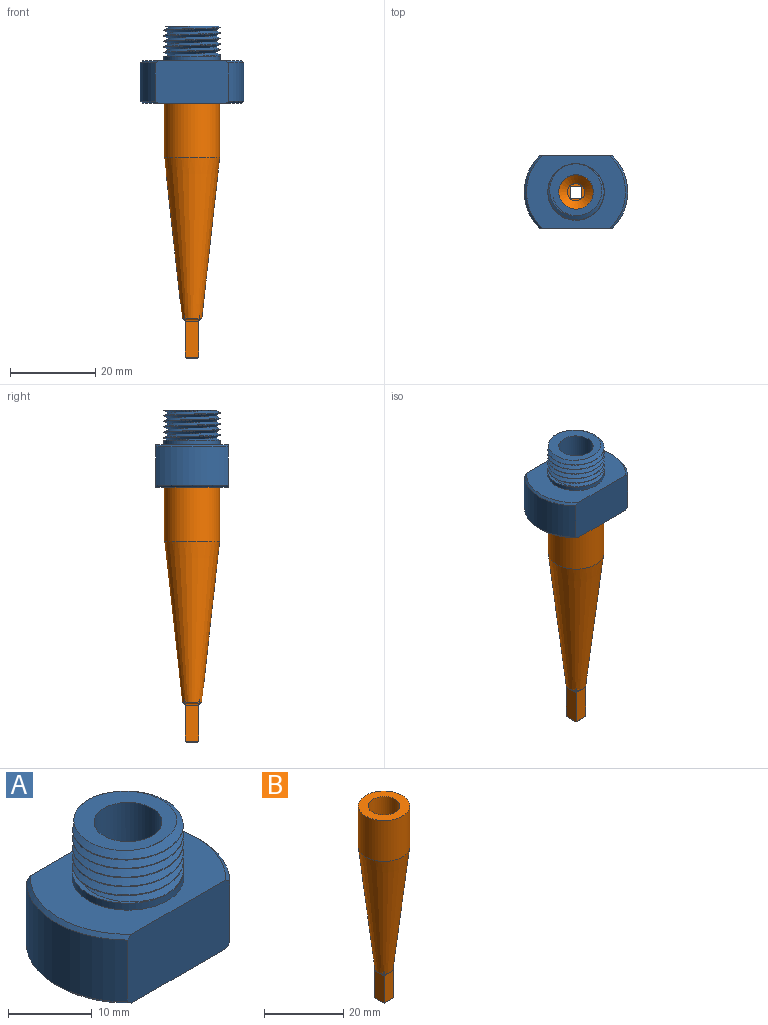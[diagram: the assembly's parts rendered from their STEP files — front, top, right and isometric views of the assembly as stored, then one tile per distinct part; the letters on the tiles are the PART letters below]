
ASSEMBLY  parts=2 mates=1
PART A: 20 faces, bbox 24.3x17.8x19 mm
  f0: plane 0.34x0.29mm, normal (0,1,0), area 0mm2, adj f11,f12,f13
  f1: cylinder r=6.58mm len=13.17mm, axis (0,0,1), area 23mm2, adj f6,f10,f11,f12,f14
  f2: cylinder r=12.12mm len=17.03mm, axis (0,0,1), area 170.5mm2, adj f7,f8,f17,f19
  f3: cylinder r=12.12mm len=17.03mm, axis (0,0,1), area 170.5mm2, adj f7,f8,f16,f18
  f4: plane 23.24x17.03mm, normal (0,0,1), area 217.8mm2, adj f7,f8,f15,f18,f19
  f5: plane 23.24x17.03mm, normal (0,0,-1), area 305.4mm2, adj f7,f8,f9,f16,f17
  f6: plane 12.24x12.19mm, normal (0,0,1), area 66mm2, adj f1,f9,f11,f12
  f7: plane 17.26x10.04mm, normal (0,-1,0), area 172.3mm2, adj f2,f3,f4,f5,f16,f17,f18,f19
  f8: plane 17.26x10.04mm, normal (0,1,0), area 172.3mm2, adj f2,f3,f4,f5,f16,f17,f18,f19
  f9: cylinder r=4.04mm len=18.18mm, axis (0,0,1), area 462.1mm2, adj f5,f6
  f10: plane 0.43x0.25mm, normal (0,1,0), area 0.1mm2, adj f1,f12,f14
  f11: bspline ~15.21x13.17mm, area 255.6mm2, adj f0,f1,f6,f12,f13,f14
  f12: bspline ~15.21x13.17mm, area 252.3mm2, adj f0,f1,f6,f10,f11,f13,f14
  f13: cylinder r=5.84mm len=10.57mm, axis (0,0,-1), area 3.4mm2, adj f0,f11,f12,f14
  f14: plane 13.34x13.34mm, normal (0,0,1), area 18.4mm2, adj f1,f10,f11,f12,f13,f15
  f15: cylinder r=6.65mm len=13.3mm, axis (0,0,-1), area 41.8mm2, adj f4,f14
  f16: cone r=12.12mm half-angle=45deg, axis (0,0,1), area 13.4mm2, adj f3,f5,f7,f8
  f17: cone r=12.12mm half-angle=45deg, axis (0,0,1), area 13.4mm2, adj f2,f5,f7,f8
  f18: cone r=11.62mm half-angle=45deg, axis (0,0,-1), area 13.4mm2, adj f3,f4,f7,f8
  f19: cone r=11.62mm half-angle=45deg, axis (0,0,-1), area 13.4mm2, adj f2,f4,f7,f8
PART B: 35 faces, bbox 13x13x59.7 mm
  f0: plane 1.15x0.07mm, normal (0,0,-1), area 0.1mm2, adj f3,f24
  f1: plane 1.15x0.07mm, normal (0,0,-1), area 0.1mm2, adj f3,f25
  f2: plane 1.15x0.07mm, normal (0,0,-1), area 0.1mm2, adj f3,f23
  f3: cone r=6.5mm half-angle=6.3deg, axis (0,0,1), area 1054.2mm2, adj f0,f1,f2,f4,f6,f22,f23,f24
  f4: cylinder r=6.5mm len=13mm, axis (0,0,1), area 516.6mm2, adj f3,f5
  f5: plane 13x13mm, normal (0,0,1), area 81.5mm2, adj f4,f11
  f6: plane 1.15x0.07mm, normal (0,0,-1), area 0.1mm2, adj f3,f22
  f7: plane 8.5x3.25mm, normal (1,0,0), area 27.3mm2, adj f8,f10,f18,f24,f28,f31
  f8: plane 8.5x3.25mm, normal (0,-1,0), area 27.3mm2, adj f7,f9,f20,f23,f30,f33
  f9: plane 8.5x3.25mm, normal (-1,0,0), area 27.3mm2, adj f8,f10,f21,f22,f26,f32
  f10: plane 8.5x3.25mm, normal (0,1,0), area 27.3mm2, adj f7,f9,f19,f25,f27,f29
  f11: cylinder r=4.04mm len=9.4mm, axis (0,0,1), area 238.6mm2, adj f5,f34
  f12: cylinder r=2.04mm len=36mm, axis (0,0,1), area 461.4mm2, adj f13,f34
  f13: plane 4.08x4.08mm, normal (0,0,1), area 5.2mm2, adj f12,f14,f15,f16,f17
  f14: plane 12.33x2.8mm, normal (-1,0,0), area 34.5mm2, adj f13,f15,f17,f18
  f15: plane 12.33x2.8mm, normal (0,1,0), area 34.5mm2, adj f13,f14,f16,f20
  f16: plane 12.33x2.8mm, normal (1,0,0), area 34.5mm2, adj f13,f15,f17,f21
  f17: plane 12.33x2.8mm, normal (0,-1,0), area 34.5mm2, adj f13,f14,f16,f19
  f18: plane 3.25x0.23mm, normal (0.71,0,-0.71), area 1mm2, adj f7,f14,f19,f20
  f19: plane 3.25x0.23mm, normal (0,0.71,-0.71), area 1mm2, adj f10,f17,f18,f21
  f20: plane 3.25x0.23mm, normal (0,-0.71,-0.71), area 1mm2, adj f8,f15,f18,f21
  f21: plane 3.25x0.23mm, normal (-0.71,0,-0.71), area 1mm2, adj f9,f16,f19,f20
  f22: cylinder r=0.6mm len=3.22mm, axis (0,-1,0), area 2.5mm2, adj f3,f6,f9,f26,f32
  f23: cylinder r=0.6mm len=3.22mm, axis (1,0,0), area 2.5mm2, adj f2,f3,f8,f30,f33
  f24: cylinder r=0.6mm len=3.22mm, axis (0,1,0), area 2.5mm2, adj f0,f3,f7,f28,f31
  f25: cylinder r=0.6mm len=3.22mm, axis (-1,0,0), area 2.5mm2, adj f1,f3,f10,f27,f29
  f26: bspline ~3.73x0.73mm, area 0.1mm2, adj f3,f9,f22,f27
  f27: bspline ~3.73x0.73mm, area 0.1mm2, adj f3,f10,f25,f26
  f28: bspline ~3.73x0.73mm, area 0.1mm2, adj f3,f7,f24,f29
  f29: bspline ~3.73x0.73mm, area 0.1mm2, adj f3,f10,f25,f28
  f30: bspline ~3.73x0.73mm, area 0.1mm2, adj f3,f8,f23,f31
  f31: bspline ~3.73x0.73mm, area 0.1mm2, adj f3,f7,f24,f30
  f32: bspline ~3.73x0.73mm, area 0.1mm2, adj f3,f9,f22,f33
  f33: bspline ~3.73x0.73mm, area 0.1mm2, adj f3,f8,f23,f32
  f34: cone r=1.04mm half-angle=45deg, axis (0,0,1), area 54mm2, adj f11,f12
PLACE A t=(-21.33,10.89,-15.87)mm
PLACE B t=(-21.33,10.89,-14.88)mm
MATE fastened B.f3 <-> A.f1  axis (0,0,1) through (-21.33,10.89,25.72)mm
